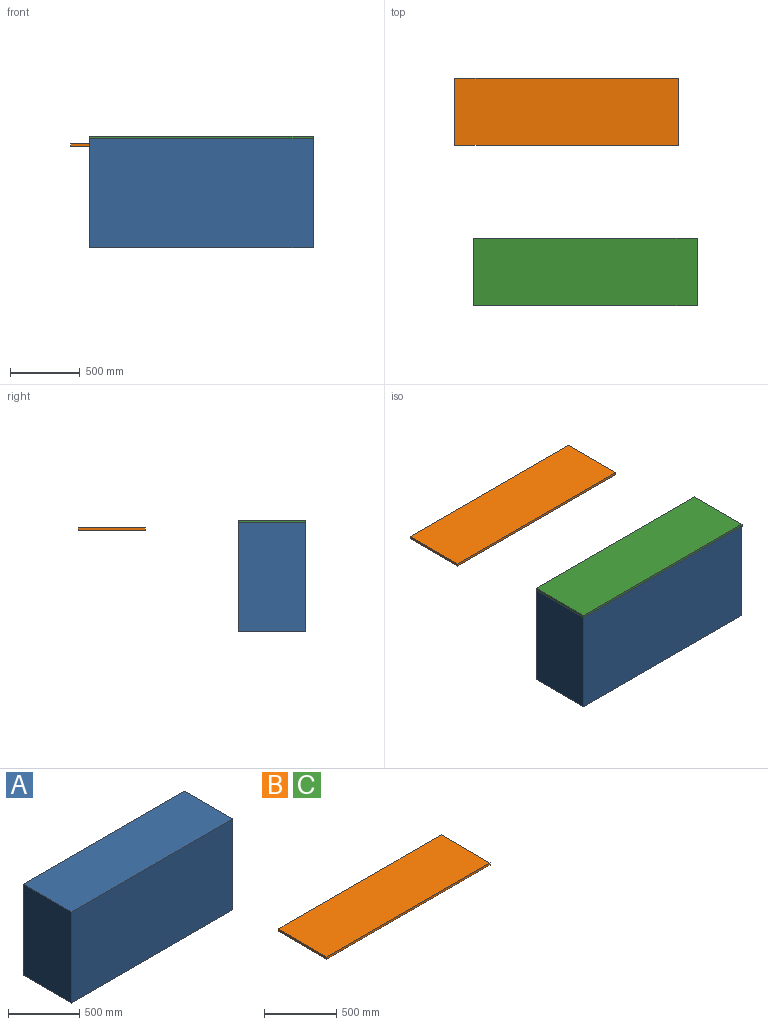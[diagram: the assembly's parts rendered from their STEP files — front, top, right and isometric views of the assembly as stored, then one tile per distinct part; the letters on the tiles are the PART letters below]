
ASSEMBLY  parts=3 mates=1
PART A: 6 faces, bbox 1600x480x780 mm
  f0: plane 780x480mm, normal (-1,0,0), area 374400mm2, adj f1,f3,f4,f5
  f1: plane 1600x780mm, normal (0,-1,0), area 1248000mm2, adj f0,f2,f4,f5
  f2: plane 780x480mm, normal (1,0,0), area 374400mm2, adj f1,f3,f4,f5
  f3: plane 1600x780mm, normal (0,1,0), area 1248000mm2, adj f0,f2,f4,f5
  f4: plane 1600x480mm, normal (0,0,1), area 768000mm2, adj f0,f1,f2,f3
  f5: plane 1600x480mm, normal (0,0,-1), area 768000mm2, adj f0,f1,f2,f3
PART B: 6 faces, bbox 1600x480x18 mm
  f0: plane 1600x18mm, normal (0,1,0), area 28800mm2, adj f1,f3,f4,f5
  f1: plane 480x18mm, normal (-1,0,0), area 8640mm2, adj f0,f2,f4,f5
  f2: plane 1600x18mm, normal (0,-1,0), area 28800mm2, adj f1,f3,f4,f5
  f3: plane 480x18mm, normal (1,0,0), area 8640mm2, adj f0,f2,f4,f5
  f4: plane 1600x480mm, normal (0,0,1), area 768000mm2, adj f0,f1,f2,f3
  f5: plane 1600x480mm, normal (0,0,-1), area 768000mm2, adj f0,f1,f2,f3
PART C: same geometry as B
PLACE A t=(0,-83.14,0)mm
PLACE B t=(-400.47,460.72,-55.24)mm
PLACE C t=(-269.53,-684.52,0)mm
MATE fastened C.f5 <-> A.f4  axis (0,0,-1) through (800,156.86,780)mm
